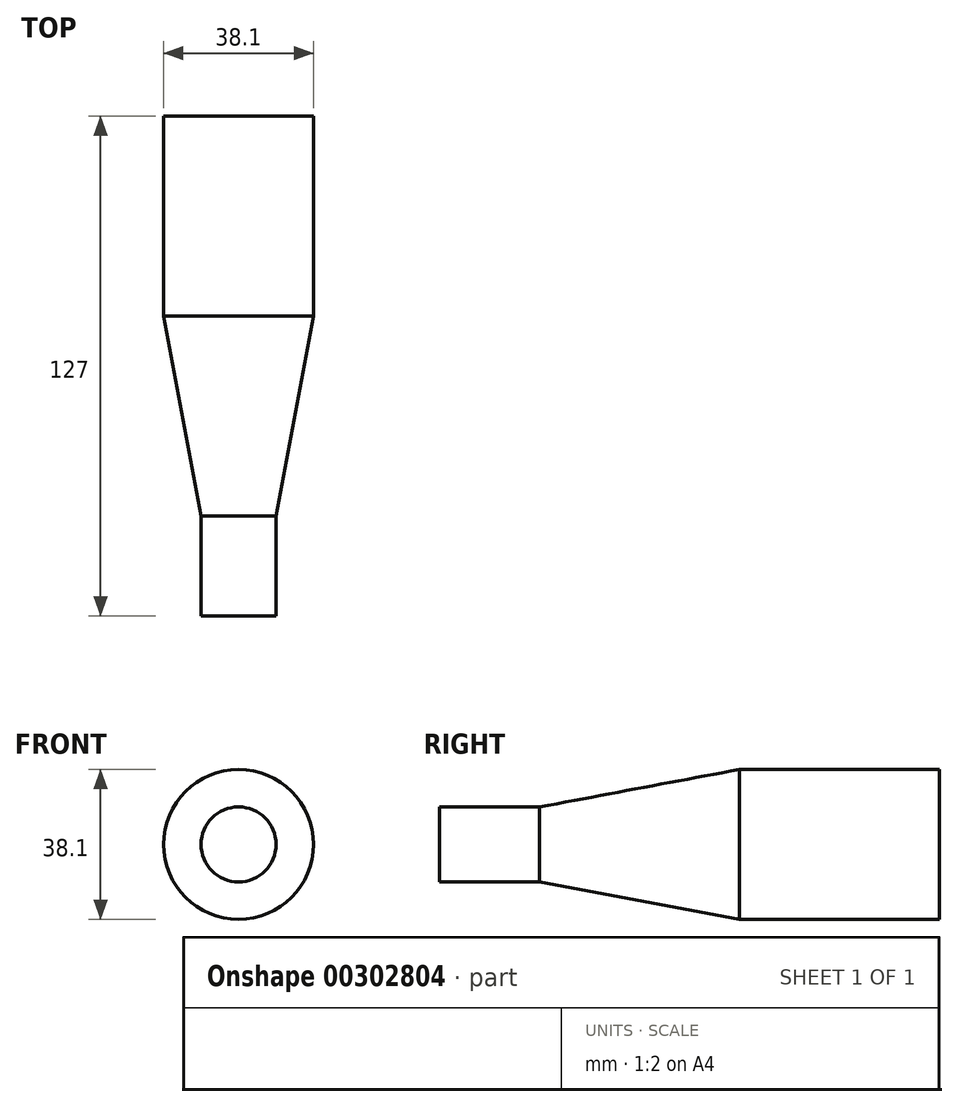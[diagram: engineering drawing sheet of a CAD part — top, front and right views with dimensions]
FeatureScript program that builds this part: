
annotation { "Feature Type Name" : "Feature", "Feature Type Description" : "" }
export const myFeature = defineFeature(function(context is Context, id is Id, definition is map)
    precondition{}
    {
        {
            var Q0;
            Q0=qCreatedBy(makeId("Right.planeOp"),FACE);
            var sketch = newSketch(context, id + "F0", { "sketchPlane" : qUnion([Q0])});
            skLineSegment(sketch, "E0", {"start": v(0, 0) * mm, "end": v(-127, 0) * mm});
            skLineSegment(sketch, "E1", {"start": v(0, 0) * mm, "end": v(0, 19.05) * mm});
            skLineSegment(sketch, "E2", {"start": v(-127, 0) * mm, "end": v(-127, 9.52) * mm});
            skLineSegment(sketch, "E3", {"start": v(0, 19.05) * mm, "end": v(-50.8, 19.05) * mm});
            skLineSegment(sketch, "E4", {"start": v(-127, 9.52) * mm, "end": v(-101.6, 9.52) * mm});
            skLineSegment(sketch, "E5", {"start": v(-101.6, 9.52) * mm, "end": v(-50.8, 19.05) * mm});
            skSolve(sketch);
        }
        {
            var Q0;
            Q0 = qSketchRegion(id + "F0", true);
            var Q1;
            Q1=sQuery(id+"F0.wireOp",EDGE,"E0");
            revolve(context, id + "F1", {"entities" : qUnion([Q0]), "axis" : qUnion([Q1]), "revolveType" : RevolveType.FULL});
        }
    });
